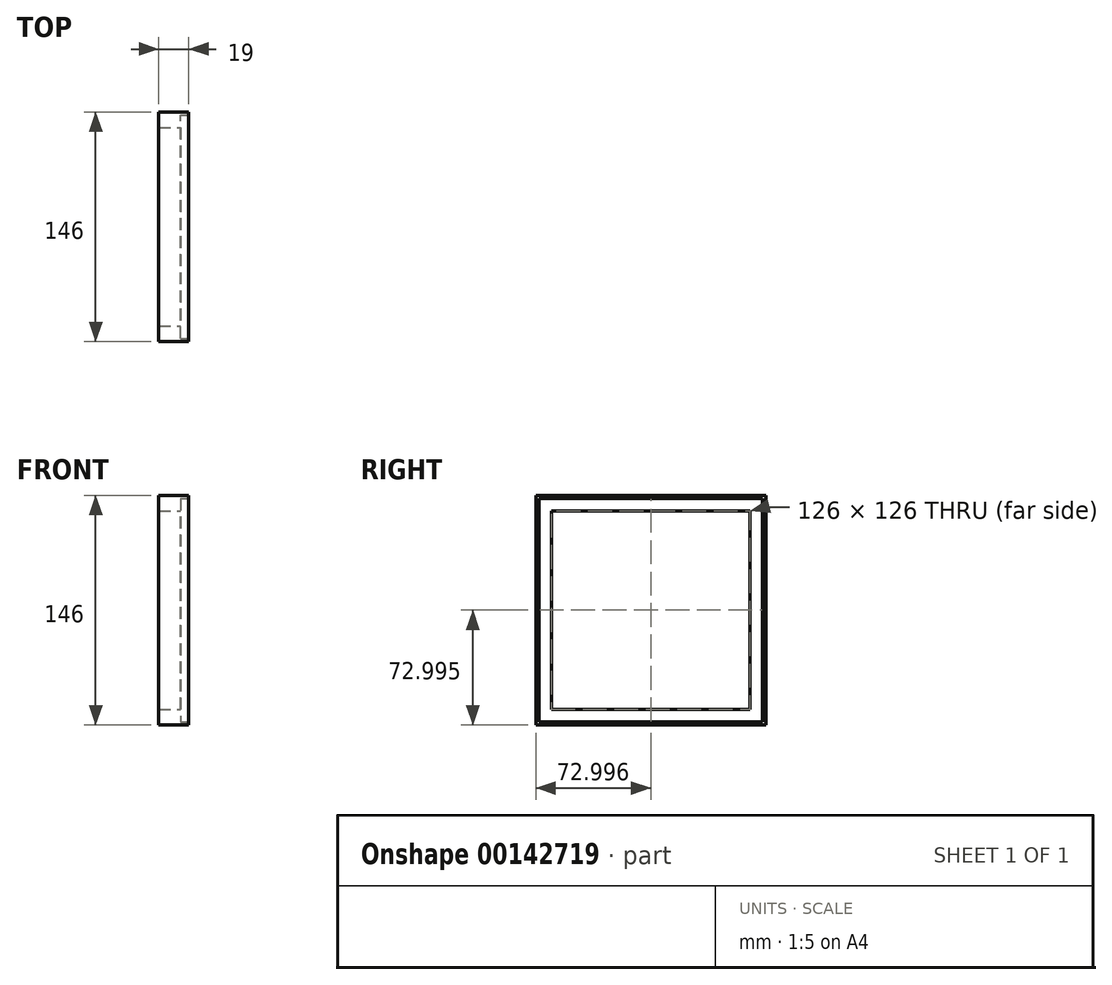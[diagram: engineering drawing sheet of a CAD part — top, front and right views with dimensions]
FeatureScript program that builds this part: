
annotation { "Feature Type Name" : "Feature", "Feature Type Description" : "" }
export const myFeature = defineFeature(function(context is Context, id is Id, definition is map)
    precondition{}
    {
        {
            var Q0;
            Q0=qCreatedBy(makeId("Right.planeOp"),FACE);
            var sketch = newSketch(context, id + "F0", { "sketchPlane" : qUnion([Q0])});
            skLineSegment(sketch, "E0.bottom", {"start": v(-55.14, 99.94) * mm, "end": v(90.86, 99.94) * mm});
            skLineSegment(sketch, "E0.top", {"start": v(-55.14, -46.06) * mm, "end": v(90.86, -46.06) * mm});
            skLineSegment(sketch, "E0.left", {"start": v(-55.14, 99.94) * mm, "end": v(-55.14, -46.06) * mm});
            skLineSegment(sketch, "E0.right", {"start": v(90.86, 99.94) * mm, "end": v(90.86, -46.06) * mm});
            skSolve(sketch);
        }
        {
            var Q0;
            Q0 = qSketchRegion(id + "F0", true);
            var Q1;
            Q1 = qSketchRegion(id + "FHTWOJbYPs5tgv8_0", true);
            extrude(context, id + "F1", {"entities" : qUnion([Q0, Q1]), "depth" : 19 * mm});
        }
        {
            var Q0;
            Q0=makeQuery(id+"F1.opExtrude","CAP_FACE",FACE,{"disambiguationData":[OSD([sQuery(id+"F0.wireOp",EDGE,"E0.bottom"),sQuery(id+"F0.wireOp",EDGE,"E0.top"),sQuery(id+"F0.wireOp",EDGE,"E0.left"),sQuery(id+"F0.wireOp",EDGE,"E0.right")])],"isStart":false});
            var sketch = newSketch(context, id + "F2", { "sketchPlane" : qUnion([Q0])});
            skLineSegment(sketch, "E1.bottom", {"start": v(-45.14, 89.94) * mm, "end": v(80.86, 89.94) * mm});
            skLineSegment(sketch, "E1.top", {"start": v(-45.14, -36.06) * mm, "end": v(80.86, -36.06) * mm});
            skLineSegment(sketch, "E1.left", {"start": v(-45.14, 89.94) * mm, "end": v(-45.14, -36.06) * mm});
            skLineSegment(sketch, "E1.right", {"start": v(80.86, 89.94) * mm, "end": v(80.86, -36.06) * mm});
            skSolve(sketch);
        }
        {
            var Q0;
            Q0 = qSketchRegion(id + "F2", true);
            extrude(context, id + "F3", {"entities" : qUnion([Q0]), "operationType" : NewBodyOperationType.REMOVE, "oppositeDirection" : true, "depth" : 25 * mm});
        }
        {
            var Q0;
            Q0=makeQuery(id+"F1.opExtrude","CAP_FACE",FACE,{"disambiguationData":[OSD([sQuery(id+"F0.wireOp",EDGE,"E0.bottom"),sQuery(id+"F0.wireOp",EDGE,"E0.top"),sQuery(id+"F0.wireOp",EDGE,"E0.left"),sQuery(id+"F0.wireOp",EDGE,"E0.right")])],"isStart":false});
            var sketch = newSketch(context, id + "F4", { "sketchPlane" : qUnion([Q0])});
            skLineSegment(sketch, "E2.bottom", {"start": v(-53.04, 97.84) * mm, "end": v(88.76, 97.84) * mm});
            skLineSegment(sketch, "E2.top", {"start": v(-53.04, -43.96) * mm, "end": v(88.76, -43.96) * mm});
            skLineSegment(sketch, "E2.left", {"start": v(-53.04, 97.84) * mm, "end": v(-53.04, -43.96) * mm});
            skLineSegment(sketch, "E2.right", {"start": v(88.76, 97.84) * mm, "end": v(88.76, -43.96) * mm});
            skSolve(sketch);
        }
        {
            var Q0;
            Q0 = qSketchRegion(id + "F4", true);
            extrude(context, id + "F5", {"entities" : qUnion([Q0]), "operationType" : NewBodyOperationType.REMOVE, "oppositeDirection" : true, "depth" : 5 * mm});
        }
    });
